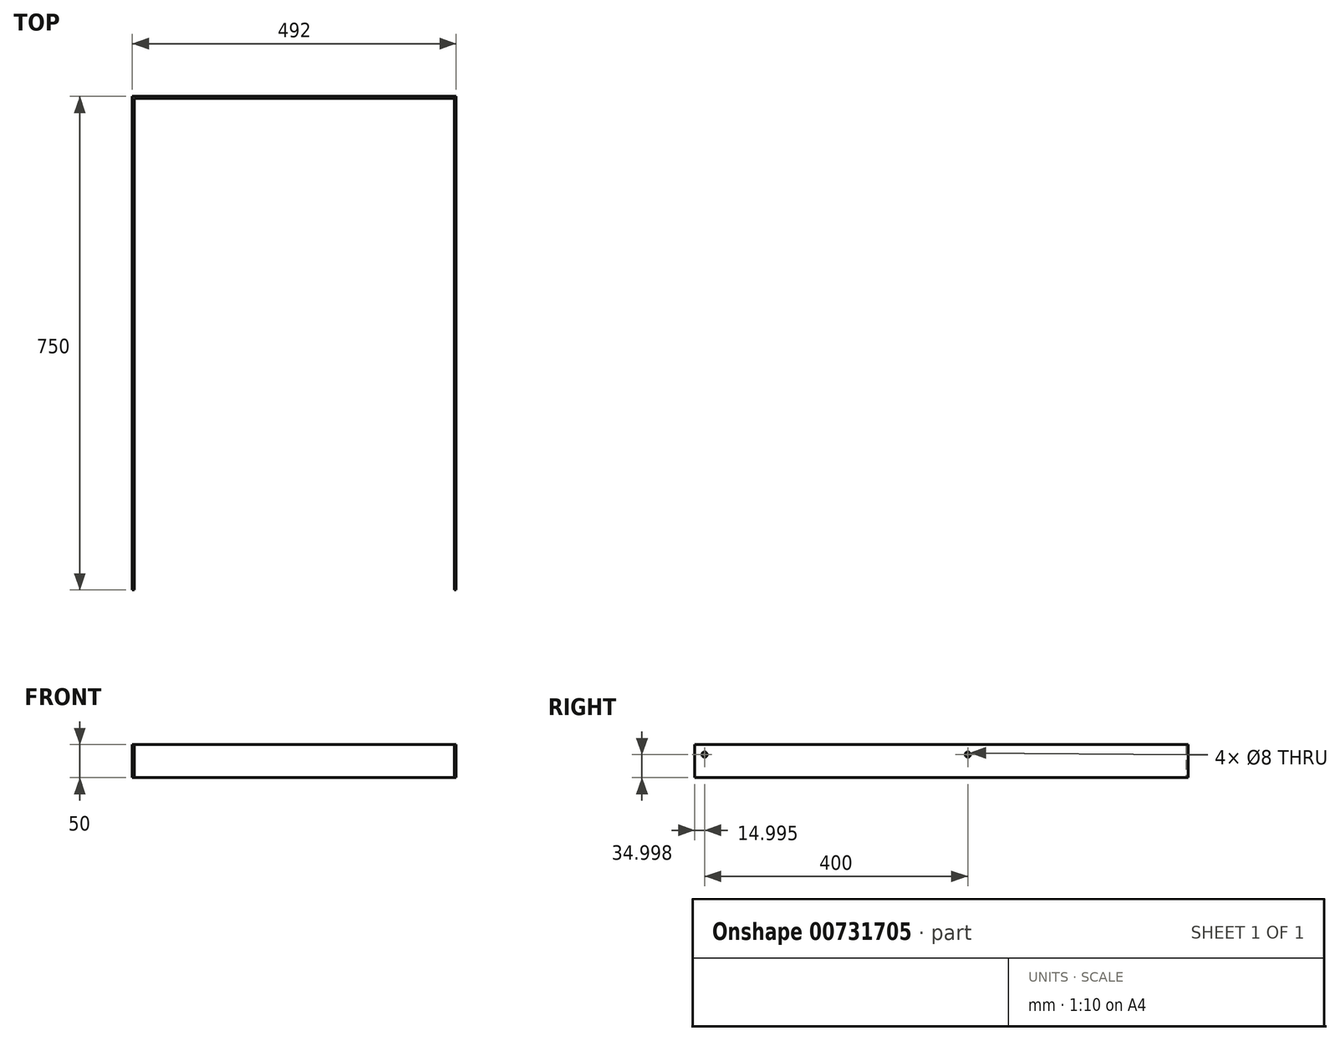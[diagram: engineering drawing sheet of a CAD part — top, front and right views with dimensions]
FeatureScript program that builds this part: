
annotation { "Feature Type Name" : "Feature", "Feature Type Description" : "" }
export const myFeature = defineFeature(function(context is Context, id is Id, definition is map)
    precondition{}
    {
        {
            var Q0;
            Q0=qCreatedBy(makeId("Right.planeOp"),FACE);
            var sketch = newSketch(context, id + "F0", { "sketchPlane" : qUnion([Q0])});
            skLineSegment(sketch, "E0.bottom", {"start": v(651.35, 273.38) * mm, "end": v(-98.65, 273.38) * mm});
            skLineSegment(sketch, "E0.top", {"start": v(651.35, 223.38) * mm, "end": v(-98.65, 223.38) * mm});
            skLineSegment(sketch, "E0.left", {"start": v(651.35, 273.38) * mm, "end": v(651.35, 223.38) * mm});
            skLineSegment(sketch, "E0.right", {"start": v(-98.65, 273.38) * mm, "end": v(-98.65, 223.38) * mm});
            skCircle(sketch, "E1", {"center": v(-83.65, 258.38) * mm, "radius": 4 * mm});
            skCircle(sketch, "E2", {"center": v(316.35, 258.38) * mm, "radius": 4 * mm});
            skLineSegment(sketch, "E3", {"start": v(648.35, 273.38) * mm, "end": v(648.35, 223.38) * mm});
            skSolve(sketch);
        }
        {
            var Q0;
            {var subQ0=sQuery(id+"F0.wireOp",EDGE,"E0.right");Q0=makeQuery(id+"F0.imprint","IMPRINT",FACE,{"disambiguationData":[TD([[makeQuery(id+"F0.imprint","IMPRINT",EDGE,{"derivedFrom":subQ0}),1.0]])]});}
            var Q1;
            {var subQ0=sQuery(id+"F0.wireOp",EDGE,"E0.left");Q1=makeQuery(id+"F0.imprint","IMPRINT",FACE,{"disambiguationData":[TD([[makeQuery(id+"F0.imprint","IMPRINT",EDGE,{"derivedFrom":subQ0}),-1.0]])]});}
            extrude(context, id + "F1", {"entities" : qUnion([Q0, Q1]), "depth" : 3 * mm, "offsetDistance" : 25 * mm});
        }
        {
            var Q0;
            {var subQ0=sQuery(id+"F0.wireOp",EDGE,"E0.left");Q0=makeQuery(id+"F0.imprint","IMPRINT",FACE,{"disambiguationData":[TD([[makeQuery(id+"F0.imprint","IMPRINT",EDGE,{"derivedFrom":subQ0}),-1.0]])]});}
            extrude(context, id + "F2", {"entities" : qUnion([Q0]), "operationType" : NewBodyOperationType.ADD, "oppositeDirection" : true, "depth" : 486 * mm, "offsetDistance" : 25 * mm});
        }
        {
            var Q0;
            Q0=makeQuery(id+"F2.opExtrude","CAP_FACE",FACE,{"disambiguationData":[OSD([sQuery(id+"F0.wireOp",EDGE,"E0.bottom"),sQuery(id+"F0.wireOp",EDGE,"E0.top"),sQuery(id+"F0.wireOp",EDGE,"E0.left"),sQuery(id+"F0.wireOp",EDGE,"E3")])],"isStart":false});
            var sketch = newSketch(context, id + "F3", { "sketchPlane" : qUnion([Q0])});
            skLineSegment(sketch, "E4.bottom", {"start": v(-651.35, 273.38) * mm, "end": v(98.65, 273.38) * mm});
            skLineSegment(sketch, "E4.top", {"start": v(-651.35, 223.38) * mm, "end": v(98.65, 223.38) * mm});
            skLineSegment(sketch, "E4.left", {"start": v(-651.35, 273.38) * mm, "end": v(-651.35, 223.38) * mm});
            skLineSegment(sketch, "E4.right", {"start": v(98.65, 273.38) * mm, "end": v(98.65, 223.38) * mm});
            skCircle(sketch, "E5", {"center": v(83.65, 258.38) * mm, "radius": 4 * mm});
            skCircle(sketch, "E6", {"center": v(-316.35, 258.38) * mm, "radius": 4 * mm});
            skSolve(sketch);
        }
        {
            var Q0;
            Q0 = qSketchRegion(id + "F3", true);
            extrude(context, id + "F4", {"entities" : qUnion([Q0]), "operationType" : NewBodyOperationType.ADD, "depth" : 3 * mm, "offsetDistance" : 25 * mm});
        }
    });
